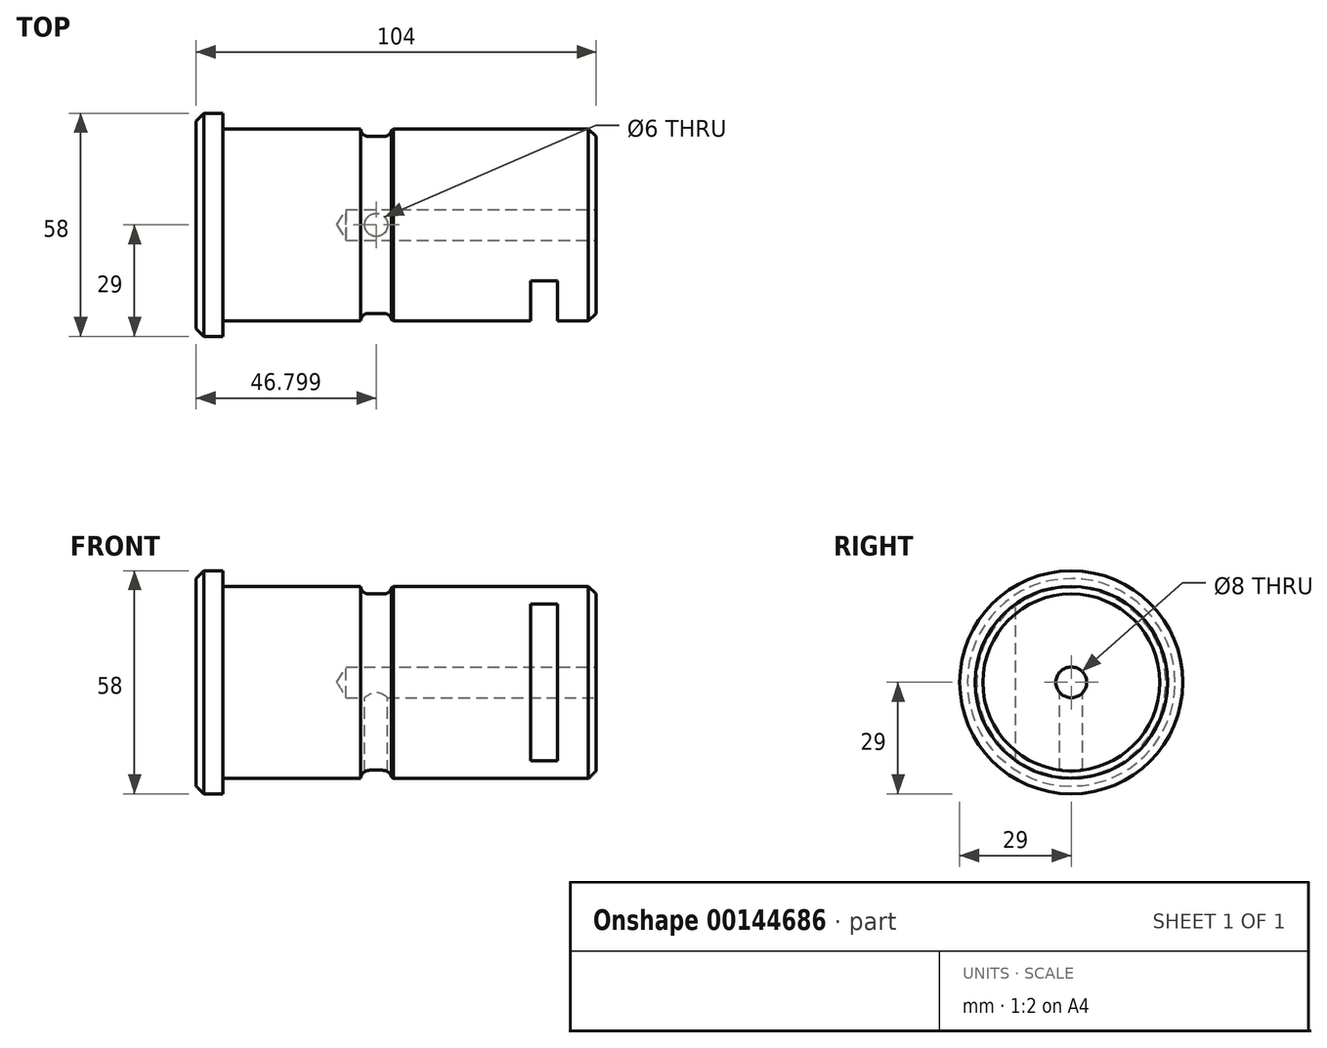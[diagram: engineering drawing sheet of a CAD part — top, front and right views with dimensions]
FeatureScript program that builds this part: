
annotation { "Feature Type Name" : "Feature", "Feature Type Description" : "" }
export const myFeature = defineFeature(function(context is Context, id is Id, definition is map)
    precondition{}
    {
        {
            var Q0;
            Q0=qCreatedBy(makeId("Right.planeOp"),FACE);
            var sketch = newSketch(context, id + "F0", { "sketchPlane" : qUnion([Q0])});
            skCircle(sketch, "E0", {"center": v(0, 0) * mm, "radius": 25 * mm});
            skSolve(sketch);
        }
        {
            var Q0;
            Q0 = qSketchRegion(id + "F0", true);
            extrude(context, id + "F1", {"entities" : qUnion([Q0]), "depth" : 97 * mm});
        }
        {
            var Q0;
            Q0=makeQuery(id+"F1.opExtrude","CAP_FACE",FACE,{"disambiguationData":[OSD([sQuery(id+"F0.wireOp",EDGE,"E0")])],"isStart":false});
            chamfer(context, id + "F2", {"entities" : qUnion([Q0]), "width" : 2 * mm, "tangentPropagation" : true});
        }
        {
            var Q0;
            Q0=qCreatedBy(makeId("Right.planeOp"),FACE);
            var sketch = newSketch(context, id + "F3", { "sketchPlane" : qUnion([Q0])});
            skCircle(sketch, "E1", {"center": v(0, 0) * mm, "radius": 29 * mm});
            skSolve(sketch);
        }
        {
            var Q0;
            Q0 = qSketchRegion(id + "F3", true);
            extrude(context, id + "F4", {"entities" : qUnion([Q0]), "operationType" : NewBodyOperationType.ADD, "oppositeDirection" : true, "depth" : 7 * mm});
        }
        {
            var Q0;
            Q0=makeQuery(id+"F4.opExtrude","CAP_FACE",FACE,{"disambiguationData":[OSD([sQuery(id+"F3.wireOp",EDGE,"E1")])],"isStart":false});
            chamfer(context, id + "F5", {"entities" : qUnion([Q0]), "width" : 2 * mm, "tangentPropagation" : true});
        }
        {
            var Q0;
            Q0=qCreatedBy(makeId("Top.planeOp"),FACE);
            var sketch = newSketch(context, id + "F6", { "sketchPlane" : qUnion([Q0])});
            skLineSegment(sketch, "E2", {"start": v(-0.2, 25) * mm, "end": v(95, 25) * mm, "construction": true});
            skLineSegment(sketch, "E3", {"start": v(95, -25) * mm, "end": v(-0.2, -25) * mm, "construction": true});
            skLineSegment(sketch, "E4", {"start": v(0, 25) * mm, "end": v(95, 25) * mm, "construction": true});
            skLineSegment(sketch, "E5", {"start": v(95, -25) * mm, "end": v(0, -25) * mm, "construction": true});
            skLineSegment(sketch, "E6", {"start": v(-0.2, 25) * mm, "end": v(-0.2, -25) * mm, "construction": true});
            skLineSegment(sketch, "E7.0", {"start": v(39.8, 25) * mm, "end": v(39.8, -25) * mm, "construction": true});
            skLineSegment(sketch, "E8", {"start": v(-24.75, 0) * mm, "end": v(141.5, 0) * mm, "construction": true});
            skLineSegment(sketch, "E9.bottom", {"start": v(35.8, 27) * mm, "end": v(43.8, 27) * mm});
            skLineSegment(sketch, "E9.top", {"start": v(37.8, 23) * mm, "end": v(41.8, 23) * mm});
            skLineSegment(sketch, "E9.left", {"start": v(35.8, 27) * mm, "end": v(35.8, 25) * mm});
            skLineSegment(sketch, "E9.right", {"start": v(43.8, 27) * mm, "end": v(43.8, 25) * mm});
            skPoint(sketch, "E9.middle", {"position": v(39.8, 25) * mm});
            skPoint(sketch, "E10.visualSharp", {"position": v(35.8, 23) * mm});
            skArc(sketch, "E10.filletArc", {"start": v(35.8, 25) * mm, "mid": v(36.38, 23.59) * mm, "end": v(37.8, 23) * mm});
            skPoint(sketch, "E11.visualSharp", {"position": v(43.8, 23) * mm});
            skArc(sketch, "E11.filletArc", {"start": v(41.8, 23) * mm, "mid": v(43.21, 23.59) * mm, "end": v(43.8, 25) * mm});
            skSolve(sketch);
        }
        {
            var Q0;
            Q0=makeQuery(id+"F6.imprint","IMPRINT",FACE,{"disambiguationData":[TD([[makeQuery(id+"F6.imprint","IMPRINT",EDGE,{"derivedFrom":sQuery(id+"F6.wireOp",EDGE,"E9.bottom")}),-1.0]])]});
            var Q1;
            Q1=sQuery(id+"F6.wireOp",EDGE,"E8");
            revolve(context, id + "F7", {"operationType" : NewBodyOperationType.REMOVE, "entities" : qUnion([Q0]), "axis" : qUnion([Q1]), "revolveType" : RevolveType.FULL, "oppositeDirection" : true});
        }
        {
            var Q0;
            Q0=qCreatedBy(makeId("Top.planeOp"),FACE);
            var sketch = newSketch(context, id + "F8", { "sketchPlane" : qUnion([Q0])});
            skLineSegment(sketch, "E12", {"start": v(0, -29) * mm, "end": v(-5, -29) * mm, "construction": true});
            skLineSegment(sketch, "E13", {"start": v(-5, 29) * mm, "end": v(0, 29) * mm, "construction": true});
            skLineSegment(sketch, "E14", {"start": v(0, 29) * mm, "end": v(0, -29) * mm, "construction": true});
            skLineSegment(sketch, "E15.0", {"start": v(80, 29) * mm, "end": v(80, -29) * mm, "construction": true});
            skLineSegment(sketch, "E16", {"start": v(43.8, 25) * mm, "end": v(95, 25) * mm, "construction": true});
            skLineSegment(sketch, "E17.bottom", {"start": v(80, -29) * mm, "end": v(87, -29) * mm});
            skLineSegment(sketch, "E17.top", {"start": v(80, -14.5) * mm, "end": v(87, -14.5) * mm});
            skLineSegment(sketch, "E17.left", {"start": v(80, -29) * mm, "end": v(80, -14.5) * mm});
            skLineSegment(sketch, "E17.right", {"start": v(87, -29) * mm, "end": v(87, -14.5) * mm});
            skSolve(sketch);
        }
        {
            var Q0;
            Q0 = qSketchRegion(id + "F8", true);
            extrude(context, id + "F9", {"entities" : qUnion([Q0]), "operationType" : NewBodyOperationType.REMOVE, "endBound" : BoundingType.SYMMETRIC, "oppositeDirection" : true, "depth" : 100 * mm});
        }
        {
            var Q0;
            Q0=makeQuery(id+"F1.opExtrude","CAP_FACE",FACE,{"disambiguationData":[OSD([sQuery(id+"F0.wireOp",EDGE,"E0")])],"isStart":false});
            var sketch = newSketch(context, id + "F10", { "sketchPlane" : qUnion([Q0])});
            skCircle(sketch, "E18.0", {"center": v(0, 0) * mm, "radius": 23 * mm, "construction": true});
            skSolve(sketch);
        }
        {
            var Q0;
            Q0=sQuery(id+"F10.wireOp",VERTEX,"E18.0.center");
            var Q1;
            Q1=makeQuery(id+"F1.opExtrude","SWEPT_BODY",BODY,{"disambiguationData":[OSD([sQuery(id+"F0.wireOp",EDGE,"E0")])]});
            hole(context, id + "F11", {"style" : HoleStyle.SIMPLE, "endStyle" : HoleEndStyle.BLIND, "standardTappedOrClearance" : lookupTablePath({ "standard" : "ISO", "size" : "8", "type" : "Drilled" }), "standardBlindInLast" : lookupTablePath({ "standard" : "ISO", "size" : "8", "type" : "Drilled" }), "holeDiameter" : 8 * mm, "holeDepth" : 65 * mm, "startFromSketch" : true, "locations" : qUnion([Q0]), "scope" : qUnion([Q1])});
        }
        {
            var Q0;
            Q0=qCreatedBy(makeId("Top.planeOp"),FACE);
            var sketch = newSketch(context, id + "F12", { "sketchPlane" : qUnion([Q0])});
            skLineSegment(sketch, "E19.0", {"start": v(37.8, 23) * mm, "end": v(37.8, -23) * mm, "construction": true});
            skLineSegment(sketch, "E20.0", {"start": v(41.8, 23) * mm, "end": v(41.8, -23) * mm, "construction": true});
            skLineSegment(sketch, "E21", {"start": v(41.8, -23) * mm, "end": v(37.8, -23) * mm, "construction": true});
            skLineSegment(sketch, "E22", {"start": v(37.8, 23) * mm, "end": v(41.8, 23) * mm, "construction": true});
            skLineSegment(sketch, "E23", {"start": v(39.8, -23) * mm, "end": v(39.8, 0) * mm, "construction": true});
            skPoint(sketch, "E24", {"position": v(39.8, 0) * mm});
            skSolve(sketch);
        }
        {
            var Q0;
            Q0=sQuery(id+"F12.wireOp",VERTEX,"E24");
            var Q1;
            Q1=makeQuery(id+"F1.opExtrude","SWEPT_BODY",BODY,{"disambiguationData":[OSD([sQuery(id+"F0.wireOp",EDGE,"E0")])]});
            hole(context, id + "F13", {"style" : HoleStyle.SIMPLE, "endStyle" : HoleEndStyle.THROUGH, "standardTappedOrClearance" : lookupTablePath({ "standard" : "ISO", "size" : "6", "type" : "Drilled" }), "standardBlindInLast" : lookupTablePath({ "standard" : "ISO", "size" : "6", "type" : "Drilled" }), "holeDiameter" : 6 * mm, "startFromSketch" : true, "locations" : qUnion([Q0]), "scope" : qUnion([Q1]), "isTappedThrough" : true});
        }
        {
            var Q0;
            Q0=makeQuery(id+"F7.boolean.opBoolean","COPY",EDGE,{"derivedFrom":makeQuery(id+"F7.opRevolve","SWEPT_EDGE",EDGE,{"disambiguationData":[OSD([sQuery(id+"F6.wireOp",EDGE,"E9.left"),sQuery(id+"F6.wireOp",EDGE,"E10.filletArc")])]})});
            var Q1;
            Q1=makeQuery(id+"F7.boolean.opBoolean","COPY",EDGE,{"derivedFrom":makeQuery(id+"F7.opRevolve","SWEPT_EDGE",EDGE,{"disambiguationData":[OSD([sQuery(id+"F6.wireOp",EDGE,"E9.right"),sQuery(id+"F6.wireOp",EDGE,"E11.filletArc")])]})});
            chamfer(context, id + "F14", {"entities" : qUnion([Q0, Q1]), "width" : .5 * mm, "tangentPropagation" : true});
        }
    });
